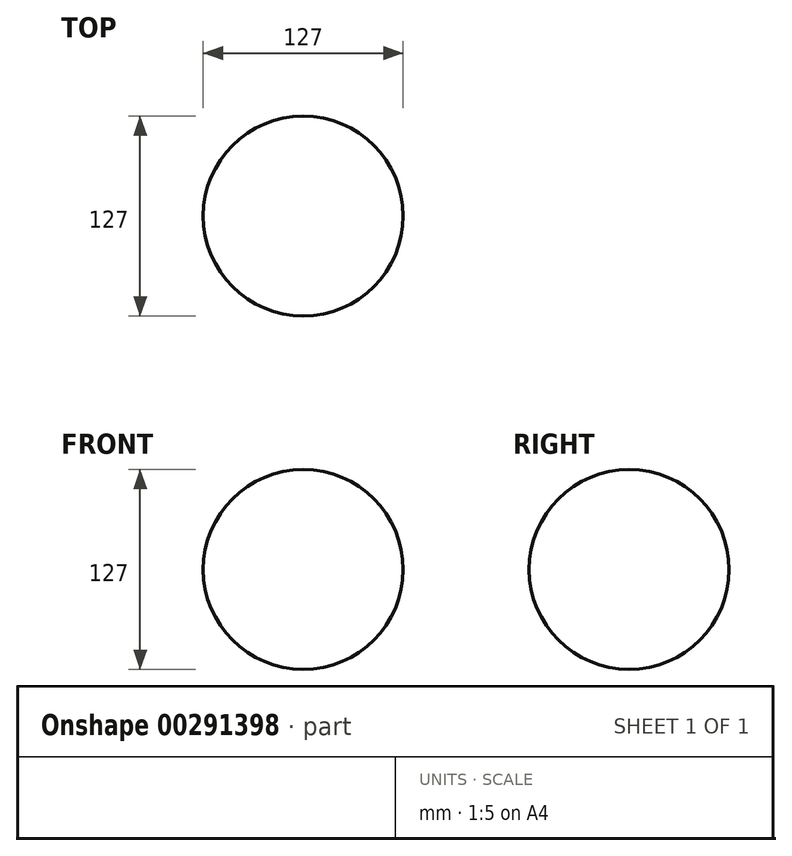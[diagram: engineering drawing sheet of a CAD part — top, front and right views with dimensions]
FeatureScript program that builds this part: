
annotation { "Feature Type Name" : "Feature", "Feature Type Description" : "" }
export const myFeature = defineFeature(function(context is Context, id is Id, definition is map)
    precondition{}
    {
        {
            var Q0;
            Q0=qCreatedBy(makeId("Front.planeOp"),FACE);
            var sketch = newSketch(context, id + "F0", { "sketchPlane" : qUnion([Q0])});
            skArc(sketch, "E0", {"start": v(63.5, 0) * mm, "mid": v(44.9, 44.9) * mm, "end": v(0, 63.5) * mm});
            skArc(sketch, "E1", {"start": v(0, -63.5) * mm, "mid": v(44.9, -44.9) * mm, "end": v(63.5, 0) * mm});
            skLineSegment(sketch, "E2", {"start": v(0, -63.5) * mm, "end": v(0, 63.5) * mm});
            skSolve(sketch);
        }
        {
            var Q0;
            Q0 = qSketchRegion(id + "F0", true);
            var Q1;
            Q1=sQuery(id+"F0.wireOp",EDGE,"E2");
            revolve(context, id + "F1", {"entities" : qUnion([Q0]), "axis" : qUnion([Q1]), "revolveType" : RevolveType.FULL});
        }
    });
